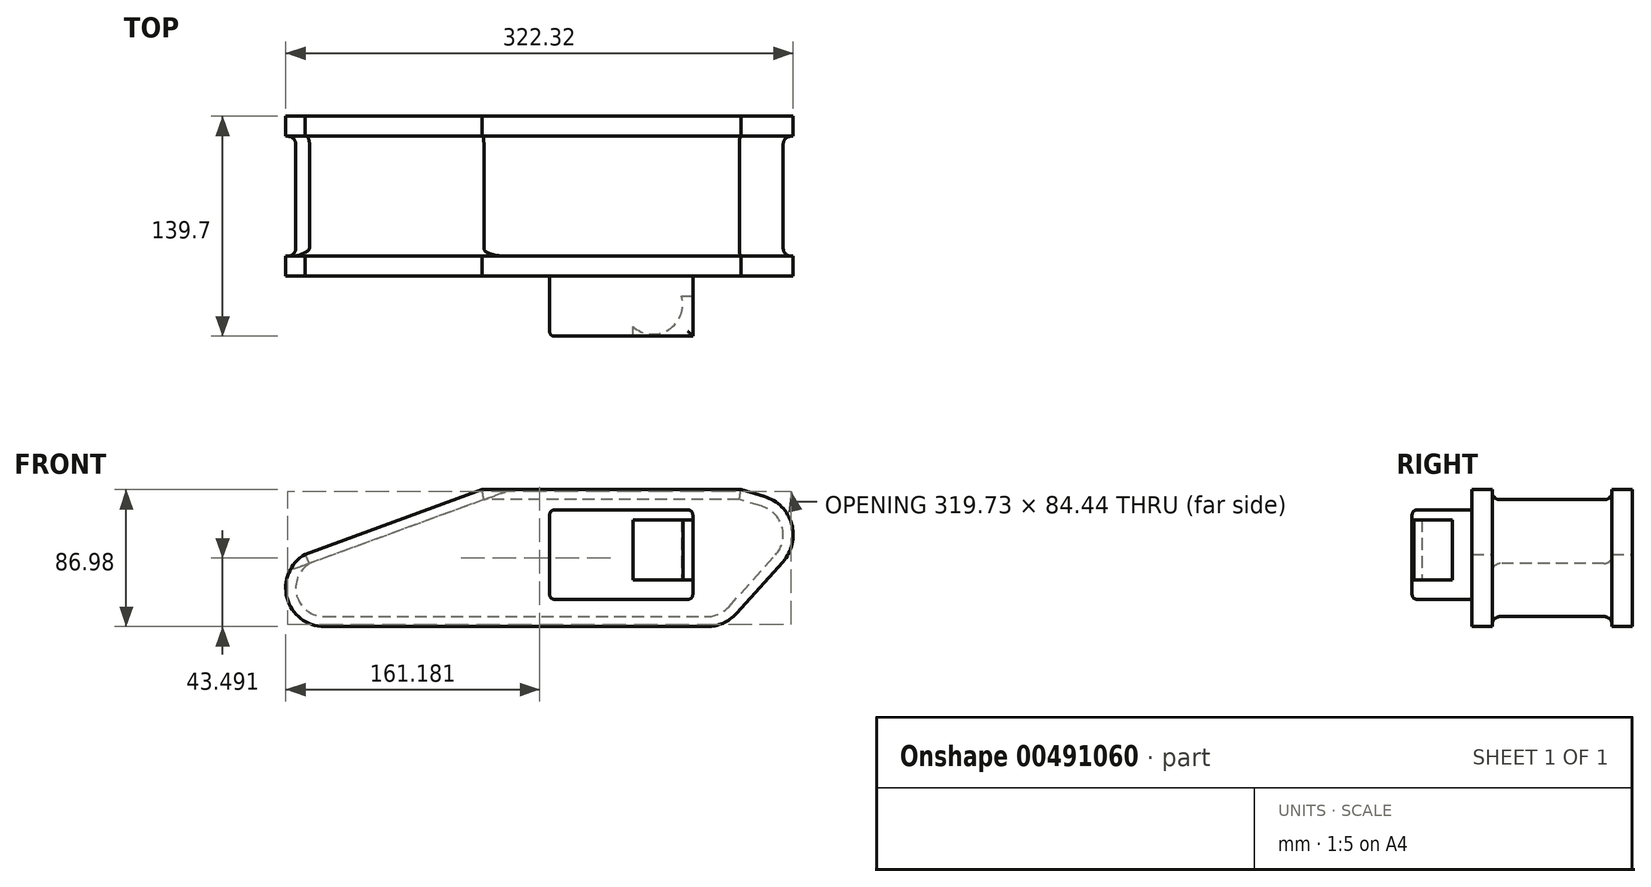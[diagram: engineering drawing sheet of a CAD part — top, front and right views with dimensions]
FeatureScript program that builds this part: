
annotation { "Feature Type Name" : "Feature", "Feature Type Description" : "" }
export const myFeature = defineFeature(function(context is Context, id is Id, definition is map)
    precondition{}
    {
        {
            var Q0;
            Q0=qCreatedBy(makeId("Front.planeOp"),FACE);
            var sketch = newSketch(context, id + "F0", { "sketchPlane" : qUnion([Q0])});
            skLineSegment(sketch, "E0", {"start": v(-21.2, 86.98) * mm, "end": v(143.12, 86.98) * mm});
            skLineSegment(sketch, "E1", {"start": v(-21.2, 86.98) * mm, "end": v(-133.57, 45.9) * mm});
            skLineSegment(sketch, "E2", {"start": v(143.12, 86.98) * mm, "end": v(158.1, 82.6) * mm});
            skLineSegment(sketch, "E3", {"start": v(169.84, 41.2) * mm, "end": v(140.22, 8.39) * mm});
            skLineSegment(sketch, "E4", {"start": v(121.37, 0) * mm, "end": v(-121.37, 0) * mm});
            skArc(sketch, "E5", {"start": v(-133.57, 45.9) * mm, "mid": v(-145.12, 18.26) * mm, "end": v(-121.37, 0) * mm});
            skPoint(sketch, "E6.visualSharp", {"position": v(196.95, 71.25) * mm});
            skArc(sketch, "E6.filletArc", {"start": v(169.84, 41.2) * mm, "mid": v(175.42, 65.15) * mm, "end": v(158.1, 82.6) * mm});
            skPoint(sketch, "E7.visualSharp", {"position": v(132.66, 0) * mm});
            skArc(sketch, "E7.filletArc", {"start": v(121.37, 0) * mm, "mid": v(131.69, 2.2) * mm, "end": v(140.22, 8.39) * mm});
            skSolve(sketch);
        }
        {
            var Q0;
            Q0=makeQuery(id+"F0.imprint","IMPRINT",FACE,{"disambiguationData":[TD([[makeQuery(id+"F0.imprint","IMPRINT",EDGE,{"derivedFrom":sQuery(id+"F0.wireOp",EDGE,"E0")}),-1.0]])]});
            extrude(context, id + "F1", {"entities" : qUnion([Q0]), "endBound" : BoundingType.SYMMETRIC, "depth" : 101.6 * mm});
        }
        {
            var Q0;
            Q0=makeQuery(id+"F1.opExtrude","CAP_FACE",FACE,{"disambiguationData":[OSD([sQuery(id+"F0.wireOp",EDGE,"E0"),sQuery(id+"F0.wireOp",EDGE,"E1"),sQuery(id+"F0.wireOp",EDGE,"E2"),sQuery(id+"F0.wireOp",EDGE,"E3"),sQuery(id+"F0.wireOp",EDGE,"E4"),sQuery(id+"F0.wireOp",EDGE,"E5"),sQuery(id+"F0.wireOp",EDGE,"E6.filletArc"),sQuery(id+"F0.wireOp",EDGE,"E7.filletArc")])],"isStart":false});
            var sketch = newSketch(context, id + "F2", { "sketchPlane" : qUnion([Q0])});
            skLineSegment(sketch, "E8.bottom", {"start": v(21.72, 74.14) * mm, "end": v(112.6, 74.14) * mm});
            skLineSegment(sketch, "E8.top", {"start": v(21.72, 17.33) * mm, "end": v(112.6, 17.33) * mm});
            skLineSegment(sketch, "E8.left", {"start": v(21.72, 74.14) * mm, "end": v(21.72, 17.33) * mm});
            skLineSegment(sketch, "E8.right", {"start": v(112.6, 74.14) * mm, "end": v(112.6, 17.33) * mm});
            skSolve(sketch);
        }
        {
            var Q0;
            Q0=makeQuery(id+"F2.imprint","IMPRINT",FACE,{"disambiguationData":[TD([[makeQuery(id+"F2.imprint","IMPRINT",EDGE,{"derivedFrom":sQuery(id+"F2.wireOp",EDGE,"E8.bottom")}),-1.0]])]});
            extrude(context, id + "F3", {"entities" : qUnion([Q0]), "operationType" : NewBodyOperationType.ADD, "depth" : 38.1 * mm});
        }
        {
            var Q0;
            Q0=makeQuery(id+"F3.opExtrude","SWEPT_FACE",FACE,{"disambiguationData":[OSD([sQuery(id+"F2.wireOp",EDGE,"E8.right")])]});
            var sketch = newSketch(context, id + "F4", { "sketchPlane" : qUnion([Q0])});
            skLineSegment(sketch, "E9.bottom", {"start": v(-88.9, 67.79) * mm, "end": v(-63.5, 67.79) * mm});
            skLineSegment(sketch, "E9.top", {"start": v(-88.9, 29.69) * mm, "end": v(-63.5, 29.69) * mm});
            skLineSegment(sketch, "E9.left", {"start": v(-88.9, 67.79) * mm, "end": v(-88.9, 29.69) * mm});
            skLineSegment(sketch, "E9.right", {"start": v(-63.5, 67.79) * mm, "end": v(-63.5, 29.69) * mm});
            skSolve(sketch);
        }
        {
            var Q0;
            Q0=makeQuery(id+"F4.imprint","IMPRINT",FACE,{"disambiguationData":[TD([[makeQuery(id+"F4.imprint","IMPRINT",EDGE,{"derivedFrom":sQuery(id+"F4.wireOp",EDGE,"E9.bottom")}),-1.0]])]});
            extrude(context, id + "F5", {"entities" : qUnion([Q0]), "operationType" : NewBodyOperationType.REMOVE, "oppositeDirection" : true, "depth" : 38.1 * mm});
        }
        {
            var Q0;
            Q0=makeQuery(id+"F5.boolean.opBoolean","COPY",FACE,{"derivedFrom":makeQuery(id+"F5.opExtrude","SWEPT_FACE",FACE,{"disambiguationData":[OSD([sQuery(id+"F4.wireOp",EDGE,"E9.top")])]})});
            var sketch = newSketch(context, id + "F6", { "sketchPlane" : qUnion([Q0])});
            skCircle(sketch, "E10", {"center": v(87.2, -68.58) * mm, "radius": 19.05 * mm});
            skSolve(sketch);
        }
        {
            var Q0;
            {var subQ0=sQuery(id+"F6.wireOp",EDGE,"E10");var subQ1=sQuery(id+"F4.wireOp",EDGE,"E9.top");var subQ4=makeQuery(id+"F5.boolean.opBoolean","COPY",EDGE,{"derivedFrom":makeQuery(id+"F5.opExtrude","CAP_EDGE",EDGE,{"disambiguationData":[OSD([subQ1])],"isStart":false})});var subQ5=makeQuery(id+"F6.imprint","INTERSECT",VERTEX,{"derivedFrom":[subQ4,subQ0]});Q0=makeQuery(id+"F6.imprint","IMPRINT",FACE,{"disambiguationData":[TD([[makeQuery(id+"F6.imprint","IMPRINT",EDGE,{"disambiguationData":[TD([[subQ5,-1.0]])],"derivedFrom":subQ0}),1.0]])]});}
            var Q1;
            Q1=makeQuery(id+"F5.boolean.opBoolean","COPY",FACE,{"derivedFrom":makeQuery(id+"F5.opExtrude","SWEPT_FACE",FACE,{"disambiguationData":[OSD([sQuery(id+"F4.wireOp",EDGE,"E9.bottom")])]})});
            extrude(context, id + "F7", {"entities" : qUnion([Q0]), "operationType" : NewBodyOperationType.ADD, "endBound" : BoundingType.UP_TO_SURFACE, "endBoundEntityFace" : qUnion([Q1]), "depth" : 25.4 * mm});
        }
        {
            var Q0;
            Q0=makeQuery(id+"F1.opExtrude","CAP_FACE",FACE,{"disambiguationData":[OSD([sQuery(id+"F0.wireOp",EDGE,"E0"),sQuery(id+"F0.wireOp",EDGE,"E1"),sQuery(id+"F0.wireOp",EDGE,"E2"),sQuery(id+"F0.wireOp",EDGE,"E3"),sQuery(id+"F0.wireOp",EDGE,"E4"),sQuery(id+"F0.wireOp",EDGE,"E5"),sQuery(id+"F0.wireOp",EDGE,"E6.filletArc"),sQuery(id+"F0.wireOp",EDGE,"E7.filletArc")])],"isStart":false});
            cPlane(context, id + "F8", {"entities" : qUnion([Q0]), "cplaneType" : CPlaneType.OFFSET, "offset" : 12.7 * mm, "oppositeDirection" : true, "width" : 152.4 * mm, "height" : 152.4 * mm});
        }
        {
            var Q0;
            Q0=qCreatedBy(id+"F8.planeOp",FACE);
            var sketch = newSketch(context, id + "F9", { "sketchPlane" : qUnion([Q0])});
            skArc(sketch, "E11.0", {"start": v(-130.84, 40.14) * mm, "mid": v(-138.91, 19.65) * mm, "end": v(-121.37, 6.35) * mm});
            skLineSegment(sketch, "E11.1", {"start": v(-20.09, 80.63) * mm, "end": v(-130.84, 40.14) * mm});
            skLineSegment(sketch, "E11.2", {"start": v(-121.37, 6.35) * mm, "end": v(121.37, 6.35) * mm});
            skLineSegment(sketch, "E11.3", {"start": v(142.21, 80.63) * mm, "end": v(-20.09, 80.63) * mm});
            skArc(sketch, "E11.4", {"start": v(121.37, 6.35) * mm, "mid": v(129.1, 8) * mm, "end": v(135.51, 12.64) * mm});
            skLineSegment(sketch, "E11.5", {"start": v(135.51, 12.64) * mm, "end": v(165.12, 45.46) * mm});
            skArc(sketch, "E11.6", {"start": v(165.12, 45.46) * mm, "mid": v(169.3, 63.42) * mm, "end": v(156.32, 76.5) * mm});
            skLineSegment(sketch, "E11.7", {"start": v(156.32, 76.5) * mm, "end": v(142.21, 80.63) * mm});
            skLineSegment(sketch, "E12.0", {"start": v(-21.2, 86.98) * mm, "end": v(-133.57, 45.9) * mm});
            skLineSegment(sketch, "E13.0", {"start": v(-21.2, 86.98) * mm, "end": v(143.12, 86.98) * mm});
            skLineSegment(sketch, "E13.1", {"start": v(143.12, 86.98) * mm, "end": v(158.1, 82.6) * mm});
            skArc(sketch, "E13.2", {"start": v(169.84, 41.2) * mm, "mid": v(175.42, 65.15) * mm, "end": v(158.1, 82.6) * mm});
            skLineSegment(sketch, "E13.3", {"start": v(169.84, 41.2) * mm, "end": v(140.22, 8.39) * mm});
            skArc(sketch, "E13.4", {"start": v(121.37, 0) * mm, "mid": v(131.69, 2.2) * mm, "end": v(140.22, 8.39) * mm});
            skLineSegment(sketch, "E13.5", {"start": v(121.37, 0) * mm, "end": v(-121.37, 0) * mm});
            skArc(sketch, "E13.6", {"start": v(-133.57, 45.9) * mm, "mid": v(-145.12, 18.26) * mm, "end": v(-121.37, 0) * mm});
            skSolve(sketch);
        }
        {
            var Q0;
            Q0 = qSketchRegion(id + "F9", true);
            extrude(context, id + "F10", {"entities" : qUnion([Q0]), "operationType" : NewBodyOperationType.REMOVE, "oppositeDirection" : true, "depth" : 76.2 * mm});
        }
        {
            var Q0;
            Q0=makeQuery(id+"F3.opExtrude","CAP_EDGE",EDGE,{"disambiguationData":[OSD([sQuery(id+"F2.wireOp",EDGE,"E8.bottom")])],"isStart":true});
            var Q1;
            Q1=makeQuery(id+"F3.opExtrude","CAP_EDGE",EDGE,{"disambiguationData":[OSD([sQuery(id+"F2.wireOp",EDGE,"E8.right")])],"isStart":true});
            var Q2;
            Q2=makeQuery(id+"F3.opExtrude","CAP_EDGE",EDGE,{"disambiguationData":[OSD([sQuery(id+"F2.wireOp",EDGE,"E8.bottom")])],"isStart":false});
            var Q3;
            Q3=makeQuery(id+"F3.opExtrude","SWEPT_EDGE",EDGE,{"disambiguationData":[OSD([sQuery(id+"F2.wireOp",EDGE,"E8.bottom"),sQuery(id+"F2.wireOp",EDGE,"E8.right")])]});
            var Q4;
            Q4=makeQuery(id+"F3.opExtrude","SWEPT_EDGE",EDGE,{"disambiguationData":[OSD([sQuery(id+"F2.wireOp",EDGE,"E8.bottom"),sQuery(id+"F2.wireOp",EDGE,"E8.left")])]});
            var Q5;
            Q5=makeQuery(id+"F3.opExtrude","SWEPT_EDGE",EDGE,{"disambiguationData":[OSD([sQuery(id+"F2.wireOp",EDGE,"E8.top"),sQuery(id+"F2.wireOp",EDGE,"E8.right")])]});
            var Q6;
            Q6=makeQuery(id+"F3.opExtrude","CAP_EDGE",EDGE,{"disambiguationData":[OSD([sQuery(id+"F2.wireOp",EDGE,"E8.top")])],"isStart":false});
            var Q7;
            Q7=makeQuery(id+"F3.opExtrude","CAP_EDGE",EDGE,{"disambiguationData":[OSD([sQuery(id+"F2.wireOp",EDGE,"E8.left")])],"isStart":false});
            var Q8;
            Q8=makeQuery(id+"F3.opExtrude","SWEPT_EDGE",EDGE,{"disambiguationData":[OSD([sQuery(id+"F2.wireOp",EDGE,"E8.top"),sQuery(id+"F2.wireOp",EDGE,"E8.left")])]});
            fillet(context, id + "F11", {"entities" : qUnion([Q0, Q1, Q2, Q3, Q4, Q5, Q6, Q7, Q8]), "radius" : 3.05 * mm, "tangentPropagation" : true, "allowEdgeOverflow" : false});
        }
        {
            var Q0;
            Q0=makeQuery(id+"F10.boolean.opBoolean","COPY",EDGE,{"derivedFrom":makeQuery(id+"F10.opExtrude","CAP_EDGE",EDGE,{"disambiguationData":[OSD([sQuery(id+"F9.wireOp",EDGE,"E11.3")])],"isStart":true})});
            var Q1;
            Q1=makeQuery(id+"F10.boolean.opBoolean","COPY",EDGE,{"derivedFrom":makeQuery(id+"F10.opExtrude","CAP_EDGE",EDGE,{"disambiguationData":[OSD([sQuery(id+"F9.wireOp",EDGE,"E11.7")])],"isStart":true})});
            var Q2;
            Q2=makeQuery(id+"F10.boolean.opBoolean","COPY",EDGE,{"derivedFrom":makeQuery(id+"F10.opExtrude","CAP_EDGE",EDGE,{"disambiguationData":[OSD([sQuery(id+"F9.wireOp",EDGE,"E11.6")])],"isStart":true})});
            var Q3;
            Q3=makeQuery(id+"F10.boolean.opBoolean","COPY",EDGE,{"derivedFrom":makeQuery(id+"F10.opExtrude","CAP_EDGE",EDGE,{"disambiguationData":[OSD([sQuery(id+"F9.wireOp",EDGE,"E11.5")])],"isStart":true})});
            var Q4;
            Q4=makeQuery(id+"F10.boolean.opBoolean","COPY",EDGE,{"derivedFrom":makeQuery(id+"F10.opExtrude","CAP_EDGE",EDGE,{"disambiguationData":[OSD([sQuery(id+"F9.wireOp",EDGE,"E11.4")])],"isStart":true})});
            var Q5;
            Q5=makeQuery(id+"F10.boolean.opBoolean","COPY",EDGE,{"derivedFrom":makeQuery(id+"F10.opExtrude","CAP_EDGE",EDGE,{"disambiguationData":[OSD([sQuery(id+"F9.wireOp",EDGE,"E11.2")])],"isStart":true})});
            var Q6;
            Q6=makeQuery(id+"F10.boolean.opBoolean","COPY",EDGE,{"derivedFrom":makeQuery(id+"F10.opExtrude","CAP_EDGE",EDGE,{"disambiguationData":[OSD([sQuery(id+"F9.wireOp",EDGE,"E11.3")])],"isStart":false})});
            var Q7;
            Q7=makeQuery(id+"F10.boolean.opBoolean","COPY",EDGE,{"derivedFrom":makeQuery(id+"F10.opExtrude","CAP_EDGE",EDGE,{"disambiguationData":[OSD([sQuery(id+"F9.wireOp",EDGE,"E11.1")])],"isStart":false})});
            var Q8;
            Q8=makeQuery(id+"F10.boolean.opBoolean","COPY",EDGE,{"derivedFrom":makeQuery(id+"F10.opExtrude","CAP_EDGE",EDGE,{"disambiguationData":[OSD([sQuery(id+"F9.wireOp",EDGE,"E11.0")])],"isStart":false})});
            var Q9;
            Q9=makeQuery(id+"F10.boolean.opBoolean","COPY",EDGE,{"derivedFrom":makeQuery(id+"F10.opExtrude","CAP_EDGE",EDGE,{"disambiguationData":[OSD([sQuery(id+"F9.wireOp",EDGE,"E11.2")])],"isStart":false})});
            fillet(context, id + "F12", {"entities" : qUnion([Q0, Q1, Q2, Q3, Q4, Q5, Q6, Q7, Q8, Q9]), "radius" : 5.08 * mm, "tangentPropagation" : true, "allowEdgeOverflow" : false});
        }
    });
